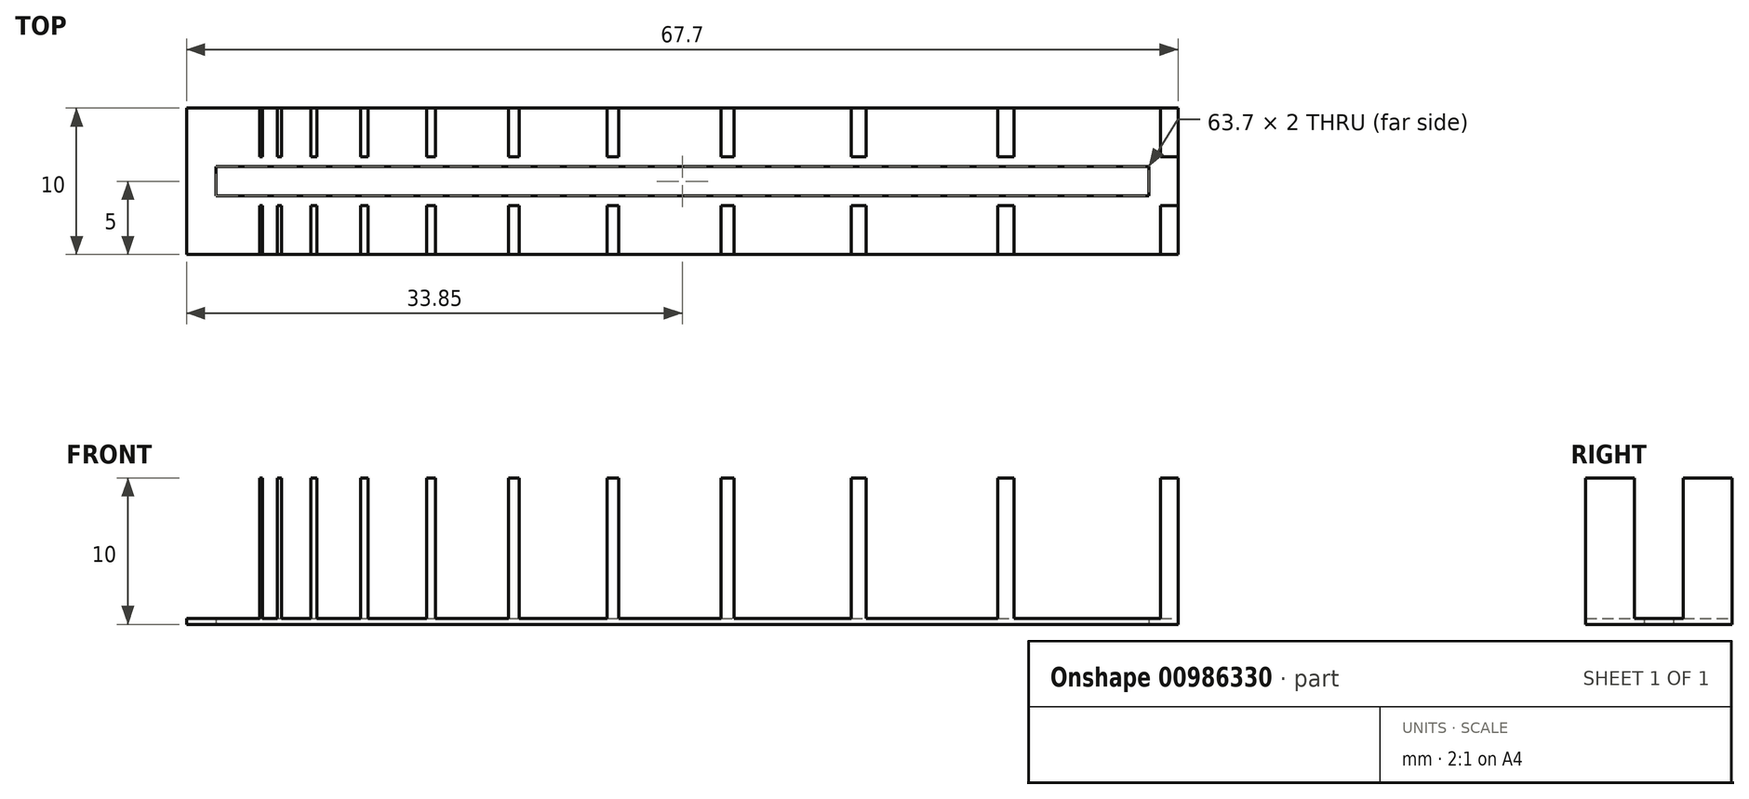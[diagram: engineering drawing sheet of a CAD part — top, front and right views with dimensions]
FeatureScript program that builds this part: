
annotation { "Feature Type Name" : "Feature", "Feature Type Description" : "" }
export const myFeature = defineFeature(function(context is Context, id is Id, definition is map)
    precondition{}
    {
        {
            var Q0;
            Q0=qCreatedBy(makeId("Top.planeOp"),FACE);
            var sketch = newSketch(context, id + "F0", { "sketchPlane" : qUnion([Q0])});
            skLineSegment(sketch, "E0.bottom", {"start": v(5.2, -5) * mm, "end": v(5, -5) * mm});
            skLineSegment(sketch, "E0.top", {"start": v(5.2, 5) * mm, "end": v(5, 5) * mm});
            skLineSegment(sketch, "E0.left", {"start": v(5.2, -5) * mm, "end": v(5.2, 5) * mm});
            skLineSegment(sketch, "E0.right", {"start": v(5, -5) * mm, "end": v(5, 5) * mm});
            skPoint(sketch, "E0.middle", {"position": v(5.1, 0) * mm});
            skLineSegment(sketch, "E1.bottom", {"start": v(6.5, -5) * mm, "end": v(6.2, -5) * mm});
            skLineSegment(sketch, "E1.top", {"start": v(6.5, 5) * mm, "end": v(6.2, 5) * mm});
            skLineSegment(sketch, "E1.left", {"start": v(6.5, -5) * mm, "end": v(6.5, 5) * mm});
            skLineSegment(sketch, "E1.right", {"start": v(6.2, -5) * mm, "end": v(6.2, 5) * mm});
            skPoint(sketch, "E1.middle", {"position": v(6.35, 0) * mm});
            skLineSegment(sketch, "E2.bottom", {"start": v(8.9, -5) * mm, "end": v(8.5, -5) * mm});
            skLineSegment(sketch, "E2.top", {"start": v(8.9, 5) * mm, "end": v(8.5, 5) * mm});
            skLineSegment(sketch, "E2.left", {"start": v(8.9, -5) * mm, "end": v(8.9, 5) * mm});
            skLineSegment(sketch, "E2.right", {"start": v(8.5, -5) * mm, "end": v(8.5, 5) * mm});
            skPoint(sketch, "E2.middle", {"position": v(8.7, 0) * mm});
            skLineSegment(sketch, "E3.bottom", {"start": v(12.4, -5) * mm, "end": v(11.9, -5) * mm});
            skLineSegment(sketch, "E3.top", {"start": v(12.4, 5) * mm, "end": v(11.9, 5) * mm});
            skLineSegment(sketch, "E3.left", {"start": v(12.4, -5) * mm, "end": v(12.4, 5) * mm});
            skLineSegment(sketch, "E3.right", {"start": v(11.9, -5) * mm, "end": v(11.9, 5) * mm});
            skPoint(sketch, "E3.middle", {"position": v(12.15, 0) * mm});
            skLineSegment(sketch, "E4.bottom", {"start": v(17, -5) * mm, "end": v(16.4, -5) * mm});
            skLineSegment(sketch, "E4.top", {"start": v(17, 5) * mm, "end": v(16.4, 5) * mm});
            skLineSegment(sketch, "E4.left", {"start": v(17, -5) * mm, "end": v(17, 5) * mm});
            skLineSegment(sketch, "E4.right", {"start": v(16.4, -5) * mm, "end": v(16.4, 5) * mm});
            skPoint(sketch, "E4.middle", {"position": v(16.7, 0) * mm});
            skLineSegment(sketch, "E5.bottom", {"start": v(22.7, -5) * mm, "end": v(22, -5) * mm});
            skLineSegment(sketch, "E5.top", {"start": v(22.7, 5) * mm, "end": v(22, 5) * mm});
            skLineSegment(sketch, "E5.left", {"start": v(22.7, -5) * mm, "end": v(22.7, 5) * mm});
            skLineSegment(sketch, "E5.right", {"start": v(22, -5) * mm, "end": v(22, 5) * mm});
            skPoint(sketch, "E5.middle", {"position": v(22.35, 0) * mm});
            skLineSegment(sketch, "E6.bottom", {"start": v(29.5, -5) * mm, "end": v(28.7, -5) * mm});
            skLineSegment(sketch, "E6.top", {"start": v(29.5, 5) * mm, "end": v(28.7, 5) * mm});
            skLineSegment(sketch, "E6.left", {"start": v(29.5, -5) * mm, "end": v(29.5, 5) * mm});
            skLineSegment(sketch, "E6.right", {"start": v(28.7, -5) * mm, "end": v(28.7, 5) * mm});
            skPoint(sketch, "E6.middle", {"position": v(29.1, 0) * mm});
            skLineSegment(sketch, "E7.bottom", {"start": v(37.4, -5) * mm, "end": v(36.5, -5) * mm});
            skLineSegment(sketch, "E7.top", {"start": v(37.4, 5) * mm, "end": v(36.5, 5) * mm});
            skLineSegment(sketch, "E7.left", {"start": v(37.4, -5) * mm, "end": v(37.4, 5) * mm});
            skLineSegment(sketch, "E7.right", {"start": v(36.5, -5) * mm, "end": v(36.5, 5) * mm});
            skPoint(sketch, "E7.middle", {"position": v(36.95, 0) * mm});
            skLineSegment(sketch, "E8.bottom", {"start": v(46.4, -5) * mm, "end": v(45.4, -5) * mm});
            skLineSegment(sketch, "E8.top", {"start": v(46.4, 5) * mm, "end": v(45.4, 5) * mm});
            skLineSegment(sketch, "E8.left", {"start": v(46.4, -5) * mm, "end": v(46.4, 5) * mm});
            skLineSegment(sketch, "E8.right", {"start": v(45.4, -5) * mm, "end": v(45.4, 5) * mm});
            skPoint(sketch, "E8.middle", {"position": v(45.9, 0) * mm});
            skLineSegment(sketch, "E9.bottom", {"start": v(56.5, -5) * mm, "end": v(55.4, -5) * mm});
            skLineSegment(sketch, "E9.top", {"start": v(56.5, 5) * mm, "end": v(55.4, 5) * mm});
            skLineSegment(sketch, "E9.left", {"start": v(56.5, -5) * mm, "end": v(56.5, 5) * mm});
            skLineSegment(sketch, "E9.right", {"start": v(55.4, -5) * mm, "end": v(55.4, 5) * mm});
            skPoint(sketch, "E9.middle", {"position": v(55.95, 0) * mm});
            skLineSegment(sketch, "E10.bottom", {"start": v(67.7, -5) * mm, "end": v(66.5, -5) * mm});
            skLineSegment(sketch, "E10.top", {"start": v(67.7, 5) * mm, "end": v(66.5, 5) * mm});
            skLineSegment(sketch, "E10.left", {"start": v(67.7, -5) * mm, "end": v(67.7, 5) * mm});
            skLineSegment(sketch, "E10.right", {"start": v(66.5, -5) * mm, "end": v(66.5, 5) * mm});
            skPoint(sketch, "E10.middle", {"position": v(67.1, 0) * mm});
            skSolve(sketch);
        }
        {
            var Q0;
            Q0 = qSketchRegion(id + "F0", true);
            extrude(context, id + "F1", {"entities" : qUnion([Q0]), "depth" : 10 * mm, "offsetDistance" : 25 * mm});
        }
        {
            var Q0;
            Q0=qCreatedBy(makeId("Top.planeOp"),FACE);
            var sketch = newSketch(context, id + "F2", { "sketchPlane" : qUnion([Q0])});
            skLineSegment(sketch, "E11.bottom", {"start": v(0, 1.67) * mm, "end": v(67.7, 1.67) * mm});
            skLineSegment(sketch, "E11.top", {"start": v(0, -1.67) * mm, "end": v(67.7, -1.67) * mm});
            skLineSegment(sketch, "E11.left", {"start": v(0, 1.67) * mm, "end": v(0, -1.67) * mm});
            skLineSegment(sketch, "E11.right", {"start": v(67.7, 1.67) * mm, "end": v(67.7, -1.67) * mm});
            skPoint(sketch, "E11.middle", {"position": v(33.85, 0) * mm});
            skSolve(sketch);
        }
        {
            var Q0;
            Q0 = qSketchRegion(id + "F2", true);
            extrude(context, id + "F3", {"entities" : qUnion([Q0]), "operationType" : NewBodyOperationType.REMOVE, "endBound" : BoundingType.THROUGH_ALL, "depth" : 25 * mm, "offsetDistance" : 25 * mm});
        }
        {
            var Q0;
            Q0=qCreatedBy(makeId("Top.planeOp"),FACE);
            var sketch = newSketch(context, id + "F4", { "sketchPlane" : qUnion([Q0])});
            skLineSegment(sketch, "E12.bottom", {"start": v(0, -5) * mm, "end": v(67.7, -5) * mm});
            skLineSegment(sketch, "E12.top", {"start": v(0, 5) * mm, "end": v(67.7, 5) * mm});
            skLineSegment(sketch, "E12.left", {"start": v(0, -5) * mm, "end": v(0, 5) * mm});
            skLineSegment(sketch, "E12.right", {"start": v(67.7, -5) * mm, "end": v(67.7, 5) * mm});
            skPoint(sketch, "E12.middle", {"position": v(33.85, 0) * mm});
            skLineSegment(sketch, "E13.bottom", {"start": v(2, -1) * mm, "end": v(65.7, -1) * mm});
            skLineSegment(sketch, "E13.top", {"start": v(2, 1) * mm, "end": v(65.7, 1) * mm});
            skLineSegment(sketch, "E13.left", {"start": v(2, -1) * mm, "end": v(2, 1) * mm});
            skLineSegment(sketch, "E13.right", {"start": v(65.7, -1) * mm, "end": v(65.7, 1) * mm});
            skSolve(sketch);
        }
        {
            var Q0;
            Q0 = qSketchRegion(id + "F4", true);
            extrude(context, id + "F5", {"entities" : qUnion([Q0]), "operationType" : NewBodyOperationType.ADD, "depth" : 0.4 * mm, "offsetDistance" : 25 * mm});
        }
    });
